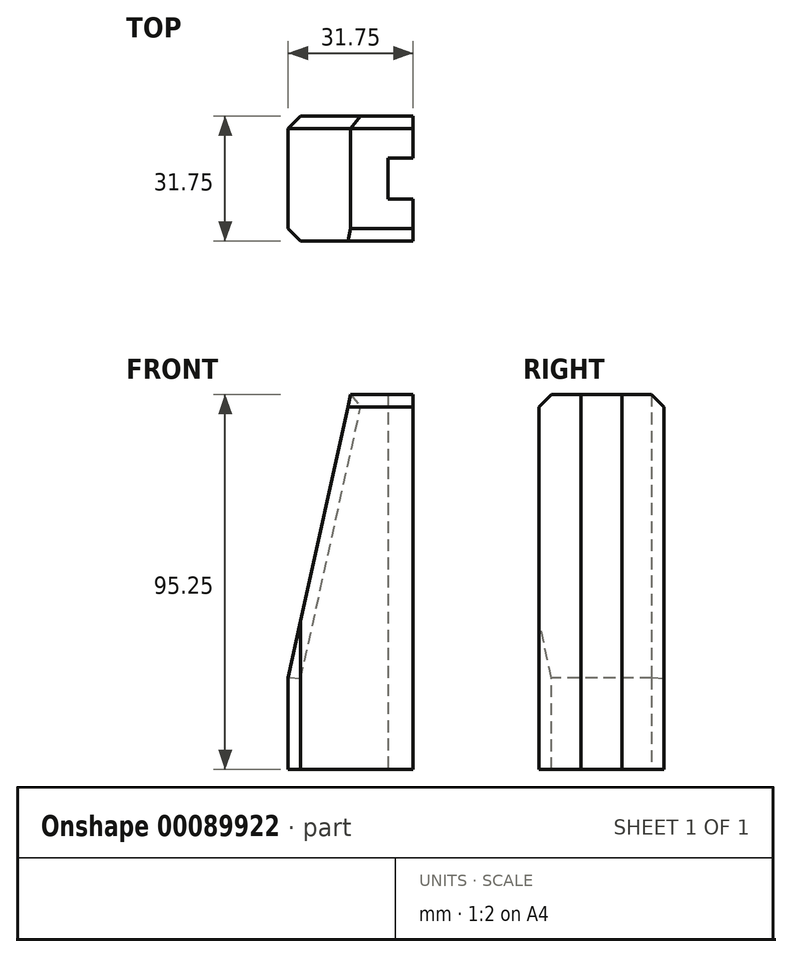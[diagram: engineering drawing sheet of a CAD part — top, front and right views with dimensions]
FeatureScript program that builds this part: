
annotation { "Feature Type Name" : "Feature", "Feature Type Description" : "" }
export const myFeature = defineFeature(function(context is Context, id is Id, definition is map)
    precondition{}
    {
        {
            var Q0;
            Q0=qCreatedBy(makeId("Top.planeOp"),FACE);
            var sketch = newSketch(context, id + "F0", { "sketchPlane" : qUnion([Q0])});
            skLineSegment(sketch, "E0.bottom", {"start": v(0, 0) * mm, "end": v(31.75, 0) * mm});
            skLineSegment(sketch, "E0.top", {"start": v(0, 31.75) * mm, "end": v(31.75, 31.75) * mm});
            skLineSegment(sketch, "E0.left", {"start": v(0, 0) * mm, "end": v(0, 31.75) * mm});
            skLineSegment(sketch, "E0.right", {"start": v(31.75, 0) * mm, "end": v(31.75, 10.67) * mm});
            skLineSegment(sketch, "E1", {"start": v(31.75, 21.08) * mm, "end": v(25.4, 21.08) * mm});
            skLineSegment(sketch, "E2", {"start": v(25.4, 21.08) * mm, "end": v(25.4, 10.67) * mm});
            skLineSegment(sketch, "E3", {"start": v(25.4, 10.67) * mm, "end": v(31.75, 10.67) * mm});
            skLineSegment(sketch, "E4.trimOffspring", {"start": v(31.75, 21.08) * mm, "end": v(31.75, 31.75) * mm});
            skSolve(sketch);
        }
        {
            var Q0;
            Q0 = qSketchRegion(id + "F0", true);
            extrude(context, id + "F1", {"entities" : qUnion([Q0]), "depth" : 95.25 * mm});
        }
        {
            var Q0;
            Q0=makeQuery(id+"F1.opExtrude","SWEPT_FACE",FACE,{"disambiguationData":[OSD([sQuery(id+"F0.wireOp",EDGE,"E0.bottom")])]});
            var sketch = newSketch(context, id + "F2", { "sketchPlane" : qUnion([Q0])});
            skLineSegment(sketch, "E5", {"start": v(0, 23.3) * mm, "end": v(15.88, 95.25) * mm});
            skSolve(sketch);
        }
        {
            var Q0;
            Q0 = qSketchRegion(id + "F2", true);
            var Q1;
            {var subQ0=sQuery(id+"F2.wireOp",EDGE,"E5");Q1=makeQuery(id+"F2.imprint","IMPRINT",FACE,{"disambiguationData":[TD([[makeQuery(id+"F2.imprint","IMPRINT",EDGE,{"derivedFrom":subQ0}),1.0]])]});}
            extrude(context, id + "F3", {"entities" : qUnion([Q0, Q1]), "operationType" : NewBodyOperationType.REMOVE, "endBound" : BoundingType.THROUGH_ALL, "oppositeDirection" : true, "depth" : 25.4 * mm});
        }
        {
            var Q0;
            Q0=makeQuery(id+"F1.opExtrude","CAP_EDGE",EDGE,{"disambiguationData":[OSD([sQuery(id+"F0.wireOp",EDGE,"E0.bottom")])],"isStart":false});
            var Q1;
            Q1=makeQuery(id+"F3.boolean.opBoolean","COPY",EDGE,{"derivedFrom":makeQuery(id+"F3.opExtrude","CAP_EDGE",EDGE,{"disambiguationData":[OSD([sQuery(id+"F2.wireOp",EDGE,"E5")])],"isStart":true})});
            var Q2;
            Q2=makeQuery(id+"F3.boolean.opBoolean","COPY",EDGE,{"derivedFrom":makeQuery(id+"F3.opExtrude","SWEPT_EDGE",EDGE,{"disambiguationData":[OSD([sQuery(id+"F0.wireOp",EDGE,"E0.bottom"),sQuery(id+"F2.wireOp",EDGE,"E5")])]})});
            var Q3;
            Q3=makeQuery(id+"F1.opExtrude","SWEPT_EDGE",EDGE,{"disambiguationData":[OSD([sQuery(id+"F0.wireOp",EDGE,"E0.bottom"),sQuery(id+"F0.wireOp",EDGE,"E0.left")])]});
            var Q4;
            Q4=makeQuery(id+"F1.opExtrude","CAP_EDGE",EDGE,{"disambiguationData":[OSD([sQuery(id+"F0.wireOp",EDGE,"E0.top")])],"isStart":false});
            var Q5;
            Q5=makeQuery(id+"F3.boolean.opBoolean","INTERSECT",EDGE,{"derivedFrom":[makeQuery(id+"F1.opExtrude","SWEPT_FACE",FACE,{"disambiguationData":[OSD([sQuery(id+"F0.wireOp",EDGE,"E0.top")])]}),makeQuery(id+"F3.opExtrude","SWEPT_FACE",FACE,{"disambiguationData":[OSD([sQuery(id+"F2.wireOp",EDGE,"E5")])]})]});
            var Q6;
            Q6=makeQuery(id+"F1.opExtrude","SWEPT_EDGE",EDGE,{"disambiguationData":[OSD([sQuery(id+"F0.wireOp",EDGE,"E0.top"),sQuery(id+"F0.wireOp",EDGE,"E0.left")])]});
            chamfer(context, id + "F4", {"entities" : qUnion([Q0, Q1, Q2, Q3, Q4, Q5, Q6]), "width" : 3.17 * mm, "tangentPropagation" : true});
        }
    });
